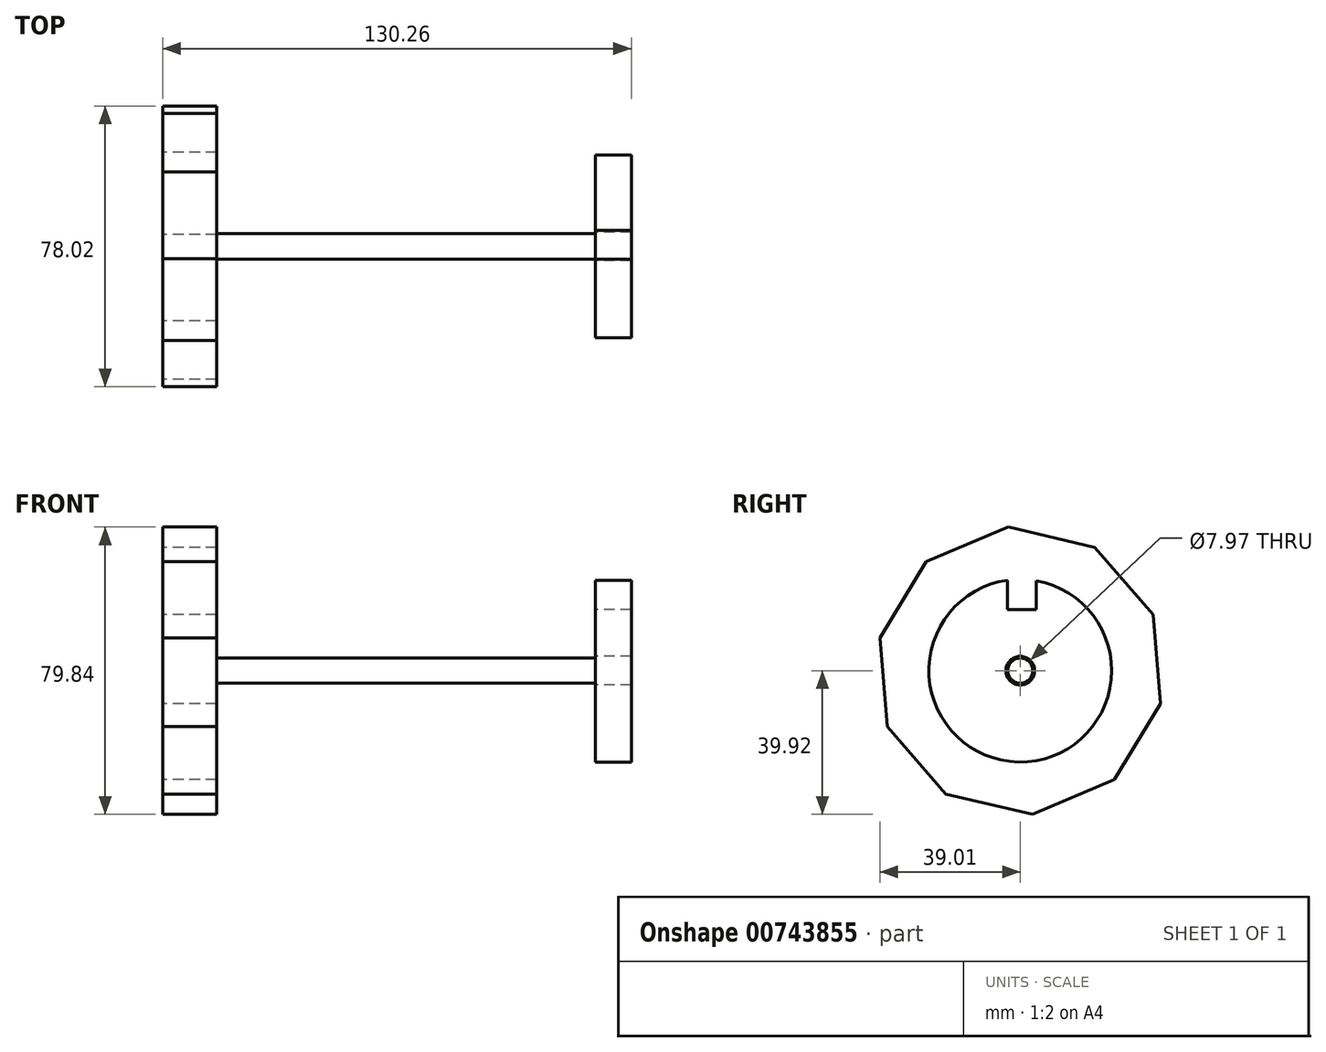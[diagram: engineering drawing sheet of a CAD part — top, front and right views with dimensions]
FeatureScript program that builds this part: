
annotation { "Feature Type Name" : "Feature", "Feature Type Description" : "" }
export const myFeature = defineFeature(function(context is Context, id is Id, definition is map)
    precondition{}
    {
        {
            var Q0;
            Q0=qCreatedBy(makeId("Right.planeOp"),FACE);
            var sketch = newSketch(context, id + "F0", { "sketchPlane" : qUnion([Q0])});
            skCircle(sketch, "E0.cCircle", {"center": v(0, 0) * mm, "radius": 38.1 * mm, "construction": true});
            skLineSegment(sketch, "E0.0", {"start": v(39, -9.13) * mm, "end": v(26.19, -30.31) * mm});
            skLineSegment(sketch, "E0.1", {"start": v(26.19, -30.31) * mm, "end": v(3.37, -39.92) * mm});
            skLineSegment(sketch, "E0.2", {"start": v(3.37, -39.92) * mm, "end": v(-20.74, -34.28) * mm});
            skLineSegment(sketch, "E0.3", {"start": v(-20.74, -34.28) * mm, "end": v(-36.92, -15.54) * mm});
            skLineSegment(sketch, "E0.4", {"start": v(-36.92, -15.54) * mm, "end": v(-39, 9.13) * mm});
            skLineSegment(sketch, "E0.5", {"start": v(-39, 9.13) * mm, "end": v(-26.19, 30.31) * mm});
            skLineSegment(sketch, "E0.6", {"start": v(-26.19, 30.31) * mm, "end": v(-3.37, 39.92) * mm});
            skLineSegment(sketch, "E0.7", {"start": v(-3.37, 39.92) * mm, "end": v(20.74, 34.28) * mm});
            skLineSegment(sketch, "E0.8", {"start": v(20.74, 34.28) * mm, "end": v(36.92, 15.54) * mm});
            skLineSegment(sketch, "E0.9", {"start": v(36.92, 15.54) * mm, "end": v(39, -9.13) * mm});
            skPoint(sketch, "E0.0.midPoint", {"position": v(32.6, -19.72) * mm});
            skSolve(sketch);
        }
        {
            var Q0;
            Q0=makeQuery(id+"F0.imprint","IMPRINT",FACE,{"disambiguationData":[TD([[makeQuery(id+"F0.imprint","IMPRINT",EDGE,{"derivedFrom":sQuery(id+"F0.wireOp",EDGE,"E0.0")}),-1.0]])]});
            extrude(context, id + "F1", {"entities" : qUnion([Q0]), "depth" : 15 * mm, "offsetDistance" : 25.4 * mm});
        }
        {
            var Q0;
            Q0=makeQuery(id+"F1.opExtrude","CAP_FACE",FACE,{"disambiguationData":[OSD([sQuery(id+"F0.wireOp",EDGE,"E0.0"),sQuery(id+"F0.wireOp",EDGE,"E0.1"),sQuery(id+"F0.wireOp",EDGE,"E0.2"),sQuery(id+"F0.wireOp",EDGE,"E0.3"),sQuery(id+"F0.wireOp",EDGE,"E0.4"),sQuery(id+"F0.wireOp",EDGE,"E0.5"),sQuery(id+"F0.wireOp",EDGE,"E0.6"),sQuery(id+"F0.wireOp",EDGE,"E0.7"),sQuery(id+"F0.wireOp",EDGE,"E0.8"),sQuery(id+"F0.wireOp",EDGE,"E0.9")])],"isStart":false});
            var sketch = newSketch(context, id + "F2", { "sketchPlane" : qUnion([Q0])});
            skCircle(sketch, "E1", {"center": v(0, 0) * mm, "radius": 3.5 * mm});
            skSolve(sketch);
        }
        {
            var Q0;
            Q0=makeQuery(id+"F2.imprint","IMPRINT",FACE,{"disambiguationData":[TD([[makeQuery(id+"F2.imprint","IMPRINT",EDGE,{"derivedFrom":sQuery(id+"F2.wireOp",EDGE,"E1")}),1.0]])]});
            extrude(context, id + "F3", {"entities" : qUnion([Q0]), "operationType" : NewBodyOperationType.ADD, "depth" : 105.26 * mm, "offsetDistance" : 25.4 * mm});
        }
        {
            var Q0;
            Q0=makeQuery(id+"F3.opExtrude","CAP_FACE",FACE,{"disambiguationData":[OSD([sQuery(id+"F2.wireOp",EDGE,"E1")])],"isStart":false});
            var sketch = newSketch(context, id + "F4", { "sketchPlane" : qUnion([Q0])});
            skCircle(sketch, "E2", {"center": v(0, 0) * mm, "radius": 25.4 * mm});
            skLineSegment(sketch, "E3", {"start": v(-3.52, 25.16) * mm, "end": v(-3.52, 17) * mm});
            skLineSegment(sketch, "E4", {"start": v(-3.52, 17) * mm, "end": v(4.48, 17) * mm});
            skLineSegment(sketch, "E5", {"start": v(4.48, 17) * mm, "end": v(4.48, 25) * mm});
            skCircle(sketch, "E6", {"center": v(0, 0) * mm, "radius": 3.48 * mm});
            skCircle(sketch, "E7.0", {"center": v(0, 0) * mm, "radius": 3.98 * mm});
            skSolve(sketch);
        }
        {
            var Q0;
            {var subQ1=sQuery(id+"F4.wireOp",EDGE,"E3");Q0=makeQuery(id+"F4.imprint","IMPRINT",FACE,{"disambiguationData":[TD([[makeQuery(id+"F4.imprint","IMPRINT",EDGE,{"derivedFrom":subQ1}),-1.0]])]});}
            extrude(context, id + "F5", {"entities" : qUnion([Q0]), "depth" : 10 * mm, "offsetDistance" : 25.4 * mm});
        }
    });
